# Revit family: Fireplace_Electric_Heatilator_SimpliFire-Allusion
name_source: partatom
category: Generic Models
revit_build: Autodesk Revit 2015 (Build: 20140606_1530(x64)
units: mm (PartAtom-declared; Revit-internal decimal feet)

## types (2) — shared parameters
Assembly Code = D3020
Construction Details = http://www.arcat.com
Default Elevation = 0' - 0"
Efficiency Ratings = as Specified
Electrical_Amperage = 13 A
Electrical_Frequency = 60 Hz
Electrical_Phase = 1
Electrical_Voltage = 120 V
Electrical_Wattage = 1500 W
Fuel Type = 120V or 240V
HVAC_BTU Output = 4800.0 Btu/h
Keynote = 10305
Manufacturer = Heatilator
Manufacturer Website = http://www.heatilator.com
Opening Height = 0' - 11 1/4"
Product Data = http://www.arcat.com
Rear Height = 1' - 5 13/16"
Rear Second Height = 1' - 7 3/8"
Revision = R1_2018-05
Sales Information = http://www.heatilator.com
Send Message = http://www.arcat.com
Specification = http://www.arcat.com
Standards Conformance = CSA 22.2 46-M1988
URL = http://www.heatilator.com
Unit Height = 1' - 8 1/4"
zero-valued in all types: Expected Lifespan (Years), Maintenance Schedule (Months), Unit Weight, Warranty Duration (Years)

## per-type parameters (varying)
| type | Description | Model | Opening Width | Rear Second Width | Rear Width | Unit Width |
| 39 x 11 Viewing Area | Heatilator Electric Fireplace - Simplifire Allusion 48 as Specified | SF-ALL48-BK | 3' - 3 3/8" | 3' - 11 1/2" | 3' - 6 13/16" | 4' - 0 7/16" |
| 51 x 11 Viewing Area | Heatilator Electric Fireplace - Simplifire Allusion 60 as Specified | SF-ALL60-BK | 4' - 3 3/16" | 4' - 11 3/8" | 4' - 6 5/8" | 5' - 0 1/4" |

## geometry (parser evidence)
native form markers: Sweep x5
no freeform markers — native parametric forms only
